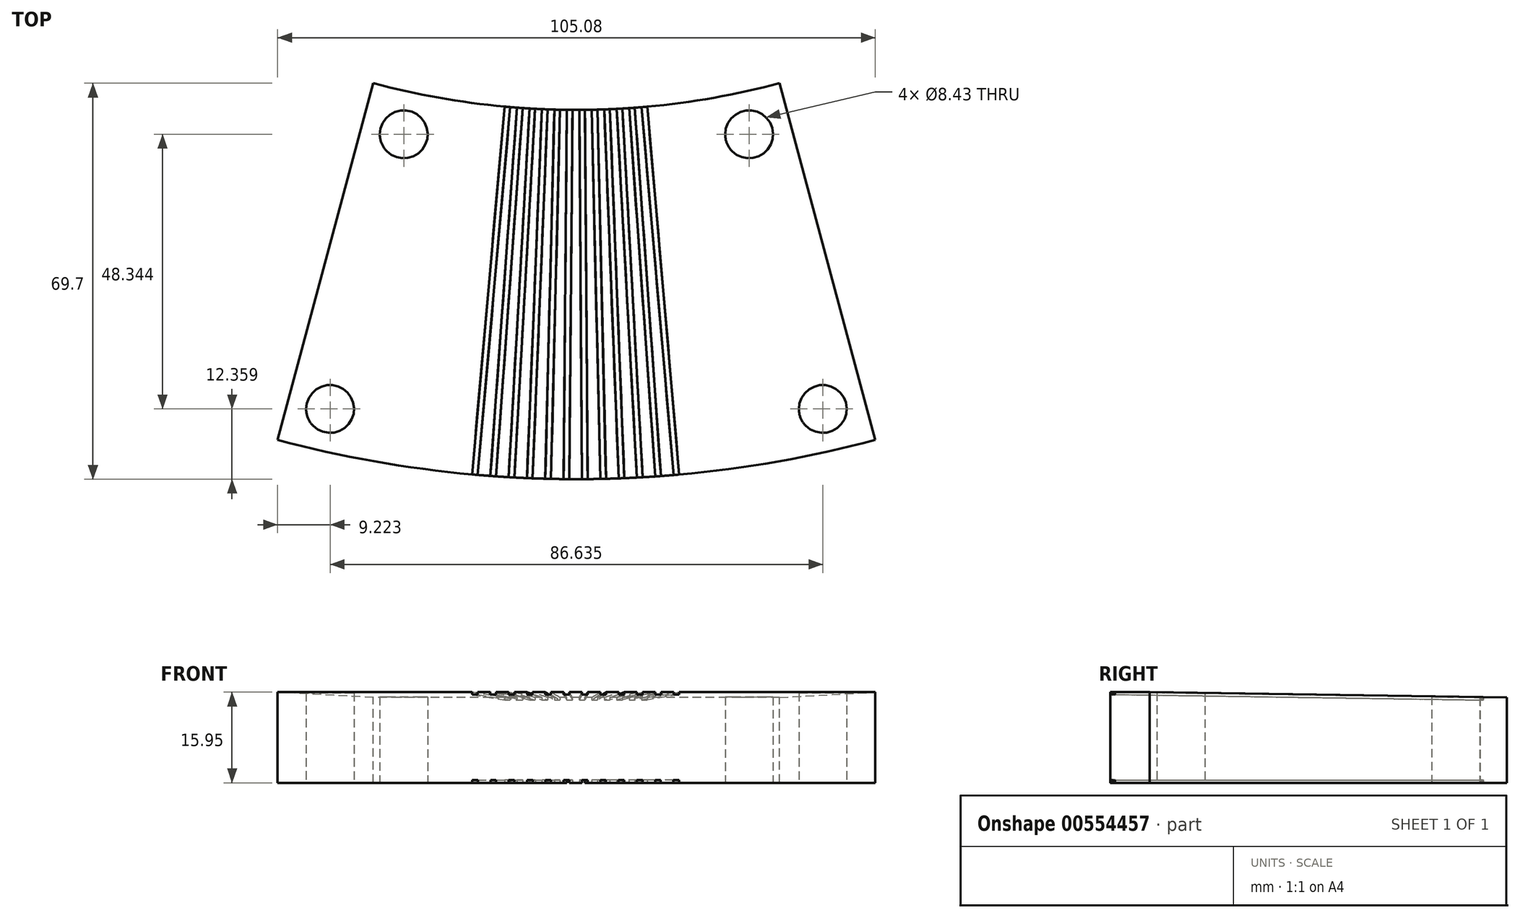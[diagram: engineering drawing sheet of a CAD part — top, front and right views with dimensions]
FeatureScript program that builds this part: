
annotation { "Feature Type Name" : "Feature", "Feature Type Description" : "" }
export const myFeature = defineFeature(function(context is Context, id is Id, definition is map)
    precondition{}
    {
        {
            var Q0;
            Q0=qCreatedBy(makeId("Right.planeOp"),FACE);
            var sketch = newSketch(context, id + "F0", { "sketchPlane" : qUnion([Q0])});
            skLineSegment(sketch, "E0", {"start": v(0, 0) * mm, "end": v(0, 15) * mm});
            skLineSegment(sketch, "E1", {"start": v(0, 15) * mm, "end": v(-65, 15.95) * mm});
            skLineSegment(sketch, "E2", {"start": v(-65, 15.95) * mm, "end": v(-65, 0) * mm});
            skLineSegment(sketch, "E3", {"start": v(-65, 0) * mm, "end": v(0, 0) * mm});
            skLineSegment(sketch, "E4", {"start": v(138, 0) * mm, "end": v(138, 35.57) * mm});
            skSolve(sketch);
        }
        {
            var Q0;
            Q0=makeQuery(id+"F0.imprint","IMPRINT",FACE,{"disambiguationData":[TD([[makeQuery(id+"F0.imprint","IMPRINT",EDGE,{"derivedFrom":sQuery(id+"F0.wireOp",EDGE,"E0")}),1.0]])]});
            var Q1;
            Q1=sQuery(id+"F0.wireOp",EDGE,"E4");
            revolve(context, id + "F1", {"entities" : qUnion([Q0]), "axis" : qUnion([Q1]), "revolveType" : RevolveType.SYMMETRIC, "angle" : 30 * degree});
        }
        {
            var Q0;
            Q0=makeQuery(id+"F1.opRevolve","SWEPT_FACE",FACE,{"disambiguationData":[OSD([sQuery(id+"F0.wireOp",EDGE,"E3")])]});
            var sketch = newSketch(context, id + "F2", { "sketchPlane" : qUnion([Q0])});
            skPoint(sketch, "E5.middle", {"position": v(0, 0) * mm});
            skLineSegment(sketch, "E6", {"start": v(0, 0) * mm, "end": v(11.98, 0) * mm});
            skLineSegment(sketch, "E7", {"start": v(11.98, 0) * mm, "end": v(-11.98, 0) * mm});
            skLineSegment(sketch, "E8.bottom", {"start": v(0, 138) * mm, "end": v(-1, 138) * mm});
            skPoint(sketch, "E8.middle", {"position": v(11.98, 0) * mm});
            skLineSegment(sketch, "E9.bottom", {"start": v(18.72, 71.9) * mm, "end": v(17.72, 71.98) * mm});
            skLineSegment(sketch, "E9.top", {"start": v(6.23, -71.98) * mm, "end": v(5.24, -71.9) * mm});
            skLineSegment(sketch, "E9.left", {"start": v(18.72, 71.9) * mm, "end": v(6.23, -71.98) * mm});
            skLineSegment(sketch, "E9.right", {"start": v(17.72, 71.98) * mm, "end": v(5.24, -71.9) * mm});
            skLineSegment(sketch, "E10", {"start": v(11.98, 0) * mm, "end": v(0, -138) * mm});
            skLineSegment(sketch, "E11.1.0", {"start": v(15.39, 72.16) * mm, "end": v(14.4, 72.23) * mm});
            skLineSegment(sketch, "E11.1.1", {"start": v(15.39, 72.16) * mm, "end": v(5.18, -71.89) * mm});
            skLineSegment(sketch, "E11.1.2", {"start": v(14.4, 72.23) * mm, "end": v(4.19, -71.82) * mm});
            skLineSegment(sketch, "E11.1.3", {"start": v(5.18, -71.89) * mm, "end": v(4.19, -71.82) * mm});
            skLineSegment(sketch, "E11.2.0", {"start": v(12.05, 72.38) * mm, "end": v(11.05, 72.43) * mm});
            skLineSegment(sketch, "E11.2.1", {"start": v(12.05, 72.38) * mm, "end": v(4.13, -71.81) * mm});
            skLineSegment(sketch, "E11.2.2", {"start": v(11.05, 72.43) * mm, "end": v(3.14, -71.76) * mm});
            skLineSegment(sketch, "E11.2.3", {"start": v(4.13, -71.81) * mm, "end": v(3.14, -71.76) * mm});
            skLineSegment(sketch, "E11.3.0", {"start": v(8.71, 72.54) * mm, "end": v(7.71, 72.58) * mm});
            skLineSegment(sketch, "E11.3.1", {"start": v(8.71, 72.54) * mm, "end": v(3.08, -71.76) * mm});
            skLineSegment(sketch, "E11.3.2", {"start": v(7.71, 72.58) * mm, "end": v(2.08, -71.72) * mm});
            skLineSegment(sketch, "E11.3.3", {"start": v(3.08, -71.76) * mm, "end": v(2.08, -71.72) * mm});
            skLineSegment(sketch, "E11.4.0", {"start": v(5.37, 72.66) * mm, "end": v(4.37, 72.68) * mm});
            skLineSegment(sketch, "E11.4.1", {"start": v(5.37, 72.66) * mm, "end": v(2.03, -71.71) * mm});
            skLineSegment(sketch, "E11.4.2", {"start": v(4.37, 72.68) * mm, "end": v(1.03, -71.7) * mm});
            skLineSegment(sketch, "E11.4.3", {"start": v(2.03, -71.71) * mm, "end": v(1.03, -71.7) * mm});
            skLineSegment(sketch, "E11.5.0", {"start": v(2.03, 72.71) * mm, "end": v(1.03, 72.72) * mm});
            skLineSegment(sketch, "E11.5.1", {"start": v(2.03, 72.71) * mm, "end": v(0.98, -71.7) * mm});
            skLineSegment(sketch, "E11.5.2", {"start": v(1.03, 72.72) * mm, "end": v(-0.02, -71.68) * mm});
            skLineSegment(sketch, "E11.5.3", {"start": v(0.98, -71.7) * mm, "end": v(-0.02, -71.68) * mm});
            skLineSegment(sketch, "E11.6.0", {"start": v(-1.32, 72.72) * mm, "end": v(-2.32, 72.71) * mm});
            skLineSegment(sketch, "E11.6.1", {"start": v(-1.32, 72.72) * mm, "end": v(-0.07, -71.68) * mm});
            skLineSegment(sketch, "E11.6.2", {"start": v(-2.32, 72.71) * mm, "end": v(-1.07, -71.7) * mm});
            skLineSegment(sketch, "E11.6.3", {"start": v(-0.07, -71.68) * mm, "end": v(-1.07, -71.7) * mm});
            skLineSegment(sketch, "E11.7.0", {"start": v(-4.66, 72.67) * mm, "end": v(-5.66, 72.65) * mm});
            skLineSegment(sketch, "E11.7.1", {"start": v(-4.66, 72.67) * mm, "end": v(-1.12, -71.7) * mm});
            skLineSegment(sketch, "E11.7.2", {"start": v(-5.66, 72.65) * mm, "end": v(-2.12, -71.72) * mm});
            skLineSegment(sketch, "E11.7.3", {"start": v(-1.12, -71.7) * mm, "end": v(-2.12, -71.72) * mm});
            skLineSegment(sketch, "E11.8.0", {"start": v(-8, 72.57) * mm, "end": v(-9, 72.53) * mm});
            skLineSegment(sketch, "E11.8.1", {"start": v(-8, 72.57) * mm, "end": v(-2.18, -71.72) * mm});
            skLineSegment(sketch, "E11.8.2", {"start": v(-9, 72.53) * mm, "end": v(-3.17, -71.76) * mm});
            skLineSegment(sketch, "E11.8.3", {"start": v(-2.18, -71.72) * mm, "end": v(-3.17, -71.76) * mm});
            skLineSegment(sketch, "E11.9.0", {"start": v(-11.34, 72.42) * mm, "end": v(-12.34, 72.36) * mm});
            skLineSegment(sketch, "E11.9.1", {"start": v(-11.34, 72.42) * mm, "end": v(-3.23, -71.76) * mm});
            skLineSegment(sketch, "E11.9.2", {"start": v(-12.34, 72.36) * mm, "end": v(-4.23, -71.82) * mm});
            skLineSegment(sketch, "E11.9.3", {"start": v(-3.23, -71.76) * mm, "end": v(-4.23, -71.82) * mm});
            skLineSegment(sketch, "E11.10.0", {"start": v(-14.68, 72.21) * mm, "end": v(-15.68, 72.14) * mm});
            skLineSegment(sketch, "E11.10.1", {"start": v(-14.68, 72.21) * mm, "end": v(-4.28, -71.82) * mm});
            skLineSegment(sketch, "E11.10.2", {"start": v(-15.68, 72.14) * mm, "end": v(-5.27, -71.9) * mm});
            skLineSegment(sketch, "E11.10.3", {"start": v(-4.28, -71.82) * mm, "end": v(-5.27, -71.9) * mm});
            skLineSegment(sketch, "E11.11.0", {"start": v(-18.01, 71.95) * mm, "end": v(-19, 71.86) * mm});
            skLineSegment(sketch, "E11.11.1", {"start": v(-18.01, 71.95) * mm, "end": v(-5.33, -71.9) * mm});
            skLineSegment(sketch, "E11.11.2", {"start": v(-19, 71.86) * mm, "end": v(-6.32, -71.99) * mm});
            skLineSegment(sketch, "E11.11.3", {"start": v(-5.33, -71.9) * mm, "end": v(-6.32, -71.99) * mm});
            skPoint(sketch, "E11.center", {"position": v(0, -138) * mm});
            skLineSegment(sketch, "E11.anchor1", {"start": v(0, -138) * mm, "end": v(5.24, -71.9) * mm, "construction": true});
            skLineSegment(sketch, "E11.anchor2", {"start": v(0, -138) * mm, "end": v(-6.32, -71.99) * mm, "construction": true});
            skSolve(sketch);
        }
        {
            var Q0;
            Q0 = qSketchRegion(id + "F2", true);
            extrude(context, id + "F3", {"entities" : qUnion([Q0]), "operationType" : NewBodyOperationType.REMOVE, "oppositeDirection" : true, "depth" : .5 * mm, "offsetDistance" : 25 * mm});
        }
        {
            var Q0;
            Q0=makeQuery(id+"F1.opRevolve","CAP_VERTEX",VERTEX,{"disambiguationData":[OSD([sQuery(id+"F0.wireOp",EDGE,"E1"),sQuery(id+"F0.wireOp",EDGE,"E2")])],"isStart":true});
            var Q1;
            Q1=makeQuery(id+"F1.opRevolve","CAP_VERTEX",VERTEX,{"disambiguationData":[OSD([sQuery(id+"F0.wireOp",EDGE,"E0"),sQuery(id+"F0.wireOp",EDGE,"E1")])],"isStart":true});
            var Q2;
            Q2=makeQuery(id+"F1.opRevolve","CAP_VERTEX",VERTEX,{"disambiguationData":[OSD([sQuery(id+"F0.wireOp",EDGE,"E0"),sQuery(id+"F0.wireOp",EDGE,"E1")])],"isStart":false});
            cPlane(context, id + "F4", {"entities" : qUnion([Q0, Q1, Q2]), "cplaneType" : CPlaneType.THREE_POINT, "offset" : 0 * mm, "width" : 150 * mm, "height" : 150 * mm});
        }
        {
            var Q0;
            Q0=qCreatedBy(id+"F4.planeOp",FACE);
            var sketch = newSketch(context, id + "F5", { "sketchPlane" : qUnion([Q0])});
            skPoint(sketch, "E12.middle", {"position": v(-0.2, 0) * mm});
            skLineSegment(sketch, "E13", {"start": v(-0.2, 0) * mm, "end": v(-12.17, 0) * mm});
            skLineSegment(sketch, "E14", {"start": v(-12.17, 0) * mm, "end": v(11.79, 0) * mm});
            skLineSegment(sketch, "E15.bottom", {"start": v(12.44, -296.36) * mm, "end": v(13.44, -296.36) * mm});
            skPoint(sketch, "E15.middle", {"position": v(-12.17, 0) * mm});
            skLineSegment(sketch, "E16.bottom", {"start": v(-19, -71.88) * mm, "end": v(-18.01, -71.97) * mm});
            skLineSegment(sketch, "E16.top", {"start": v(-6.32, 71.97) * mm, "end": v(-5.33, 71.88) * mm});
            skLineSegment(sketch, "E16.left", {"start": v(-19, -71.88) * mm, "end": v(-6.32, 71.97) * mm});
            skLineSegment(sketch, "E16.right", {"start": v(-18.01, -71.97) * mm, "end": v(-5.33, 71.88) * mm});
            skLineSegment(sketch, "E17", {"start": v(-12.17, 0) * mm, "end": v(0, 137.98) * mm});
            skLineSegment(sketch, "E18.1.0", {"start": v(-15.68, -72.16) * mm, "end": v(-14.68, -72.23) * mm});
            skLineSegment(sketch, "E18.1.1", {"start": v(-15.68, -72.16) * mm, "end": v(-5.28, 71.88) * mm});
            skLineSegment(sketch, "E18.1.2", {"start": v(-14.68, -72.23) * mm, "end": v(-4.28, 71.8) * mm});
            skLineSegment(sketch, "E18.1.3", {"start": v(-5.28, 71.88) * mm, "end": v(-4.28, 71.8) * mm});
            skLineSegment(sketch, "E18.2.0", {"start": v(-12.34, -72.38) * mm, "end": v(-11.34, -72.43) * mm});
            skLineSegment(sketch, "E18.2.1", {"start": v(-12.34, -72.38) * mm, "end": v(-4.23, 71.8) * mm});
            skLineSegment(sketch, "E18.2.2", {"start": v(-11.34, -72.43) * mm, "end": v(-3.23, 71.75) * mm});
            skLineSegment(sketch, "E18.2.3", {"start": v(-4.23, 71.8) * mm, "end": v(-3.23, 71.75) * mm});
            skLineSegment(sketch, "E18.3.0", {"start": v(-9, -72.55) * mm, "end": v(-8, -72.59) * mm});
            skLineSegment(sketch, "E18.3.1", {"start": v(-9, -72.55) * mm, "end": v(-3.18, 71.74) * mm});
            skLineSegment(sketch, "E18.3.2", {"start": v(-8, -72.59) * mm, "end": v(-2.18, 71.7) * mm});
            skLineSegment(sketch, "E18.3.3", {"start": v(-3.18, 71.74) * mm, "end": v(-2.18, 71.7) * mm});
            skLineSegment(sketch, "E18.4.0", {"start": v(-5.66, -72.66) * mm, "end": v(-4.66, -72.69) * mm});
            skLineSegment(sketch, "E18.4.1", {"start": v(-5.66, -72.66) * mm, "end": v(-2.12, 71.7) * mm});
            skLineSegment(sketch, "E18.4.2", {"start": v(-4.66, -72.69) * mm, "end": v(-1.12, 71.68) * mm});
            skLineSegment(sketch, "E18.4.3", {"start": v(-2.12, 71.7) * mm, "end": v(-1.12, 71.68) * mm});
            skLineSegment(sketch, "E18.5.0", {"start": v(-2.32, -72.73) * mm, "end": v(-1.32, -72.74) * mm});
            skLineSegment(sketch, "E18.5.1", {"start": v(-2.32, -72.73) * mm, "end": v(-1.07, 71.68) * mm});
            skLineSegment(sketch, "E18.5.2", {"start": v(-1.32, -72.74) * mm, "end": v(-0.07, 71.67) * mm});
            skLineSegment(sketch, "E18.5.3", {"start": v(-1.07, 71.68) * mm, "end": v(-0.07, 71.67) * mm});
            skLineSegment(sketch, "E18.6.0", {"start": v(1.03, -72.74) * mm, "end": v(2.03, -72.73) * mm});
            skLineSegment(sketch, "E18.6.1", {"start": v(1.03, -72.74) * mm, "end": v(-0.02, 71.67) * mm});
            skLineSegment(sketch, "E18.6.2", {"start": v(2.03, -72.73) * mm, "end": v(0.98, 71.67) * mm});
            skLineSegment(sketch, "E18.6.3", {"start": v(-0.02, 71.67) * mm, "end": v(0.98, 71.67) * mm});
            skLineSegment(sketch, "E18.7.0", {"start": v(4.37, -72.7) * mm, "end": v(5.37, -72.67) * mm});
            skLineSegment(sketch, "E18.7.1", {"start": v(4.37, -72.7) * mm, "end": v(1.03, 71.68) * mm});
            skLineSegment(sketch, "E18.7.2", {"start": v(5.37, -72.67) * mm, "end": v(2.03, 71.7) * mm});
            skLineSegment(sketch, "E18.7.3", {"start": v(1.03, 71.68) * mm, "end": v(2.03, 71.7) * mm});
            skLineSegment(sketch, "E18.8.0", {"start": v(7.71, -72.6) * mm, "end": v(8.71, -72.56) * mm});
            skLineSegment(sketch, "E18.8.1", {"start": v(7.71, -72.6) * mm, "end": v(2.08, 71.7) * mm});
            skLineSegment(sketch, "E18.8.2", {"start": v(8.71, -72.56) * mm, "end": v(3.08, 71.74) * mm});
            skLineSegment(sketch, "E18.8.3", {"start": v(2.08, 71.7) * mm, "end": v(3.08, 71.74) * mm});
            skLineSegment(sketch, "E18.9.0", {"start": v(11.05, -72.45) * mm, "end": v(12.05, -72.4) * mm});
            skLineSegment(sketch, "E18.9.1", {"start": v(11.05, -72.45) * mm, "end": v(3.14, 71.74) * mm});
            skLineSegment(sketch, "E18.9.2", {"start": v(12.05, -72.4) * mm, "end": v(4.13, 71.8) * mm});
            skLineSegment(sketch, "E18.9.3", {"start": v(3.14, 71.74) * mm, "end": v(4.13, 71.8) * mm});
            skLineSegment(sketch, "E18.10.0", {"start": v(14.39, -72.25) * mm, "end": v(15.39, -72.18) * mm});
            skLineSegment(sketch, "E18.10.1", {"start": v(14.39, -72.25) * mm, "end": v(4.19, 71.8) * mm});
            skLineSegment(sketch, "E18.10.2", {"start": v(15.39, -72.18) * mm, "end": v(5.18, 71.87) * mm});
            skLineSegment(sketch, "E18.10.3", {"start": v(4.19, 71.8) * mm, "end": v(5.18, 71.87) * mm});
            skLineSegment(sketch, "E18.11.0", {"start": v(17.72, -72) * mm, "end": v(18.72, -71.9) * mm});
            skLineSegment(sketch, "E18.11.1", {"start": v(17.72, -72) * mm, "end": v(5.24, 71.87) * mm});
            skLineSegment(sketch, "E18.11.2", {"start": v(18.72, -71.9) * mm, "end": v(6.23, 71.96) * mm});
            skLineSegment(sketch, "E18.11.3", {"start": v(5.24, 71.87) * mm, "end": v(6.23, 71.96) * mm});
            skPoint(sketch, "E18.center", {"position": v(0, 137.98) * mm});
            skLineSegment(sketch, "E18.anchor1", {"start": v(0, 137.98) * mm, "end": v(-5.33, 71.88) * mm, "construction": true});
            skLineSegment(sketch, "E18.anchor2", {"start": v(0, 137.98) * mm, "end": v(6.23, 71.96) * mm, "construction": true});
            skSolve(sketch);
        }
        {
            var Q0;
            Q0 = qSketchRegion(id + "F5", true);
            extrude(context, id + "F6", {"entities" : qUnion([Q0]), "operationType" : NewBodyOperationType.REMOVE, "oppositeDirection" : true, "depth" : .5 * mm, "offsetDistance" : 25 * mm});
        }
        {
            var Q0;
            Q0=qCreatedBy(makeId("Top.planeOp"),FACE);
            var sketch = newSketch(context, id + "F7", { "sketchPlane" : qUnion([Q0])});
            skCircle(sketch, "E19", {"center": v(-30.36, -4.3) * mm, "radius": 7.5 * mm});
            skCircle(sketch, "E20", {"center": v(-43.32, -52.64) * mm, "radius": 7.5 * mm});
            skCircle(sketch, "E21", {"center": v(43.32, -52.64) * mm, "radius": 7.5 * mm});
            skCircle(sketch, "E22", {"center": v(30.36, -4.3) * mm, "radius": 7.5 * mm});
            skSolve(sketch);
        }
        {
            var Q0;
            Q0=sQuery(id+"F7.wireOp",VERTEX,"E21.center");
            var Q1;
            Q1=sQuery(id+"F7.wireOp",VERTEX,"E20.center");
            var Q2;
            Q2=sQuery(id+"F7.wireOp",VERTEX,"E19.center");
            var Q3;
            Q3=sQuery(id+"F7.wireOp",VERTEX,"E22.center");
            var Q4;
            Q4=makeQuery(id+"F1.opRevolve","SWEPT_BODY",BODY,{"disambiguationData":[OSD([sQuery(id+"F0.wireOp",EDGE,"E0"),sQuery(id+"F0.wireOp",EDGE,"E1"),sQuery(id+"F0.wireOp",EDGE,"E2"),sQuery(id+"F0.wireOp",EDGE,"E3")])]});
            hole(context, id + "F8", {"style" : HoleStyle.SIMPLE, "endStyle" : HoleEndStyle.THROUGH, "oppositeDirection" : true, "standardTappedOrClearance" : lookupTablePath({ "standard" : "ANSI", "fit" : "Normal (ASME)", "size" : "5/16", "type" : "Clearance" }), "standardBlindInLast" : lookupTablePath({ "fit" : "Free", "standard" : "ANSI", "size" : "5/16", "type" : "Clearance" }), "holeDiameter" : 8.43 * mm, "isTappedThrough" : true, "tappedDepth" : 12 * mm, "tapClearance" : 3, "locations" : qUnion([Q0, Q1, Q2, Q3]), "scope" : qUnion([Q4])});
        }
    });
